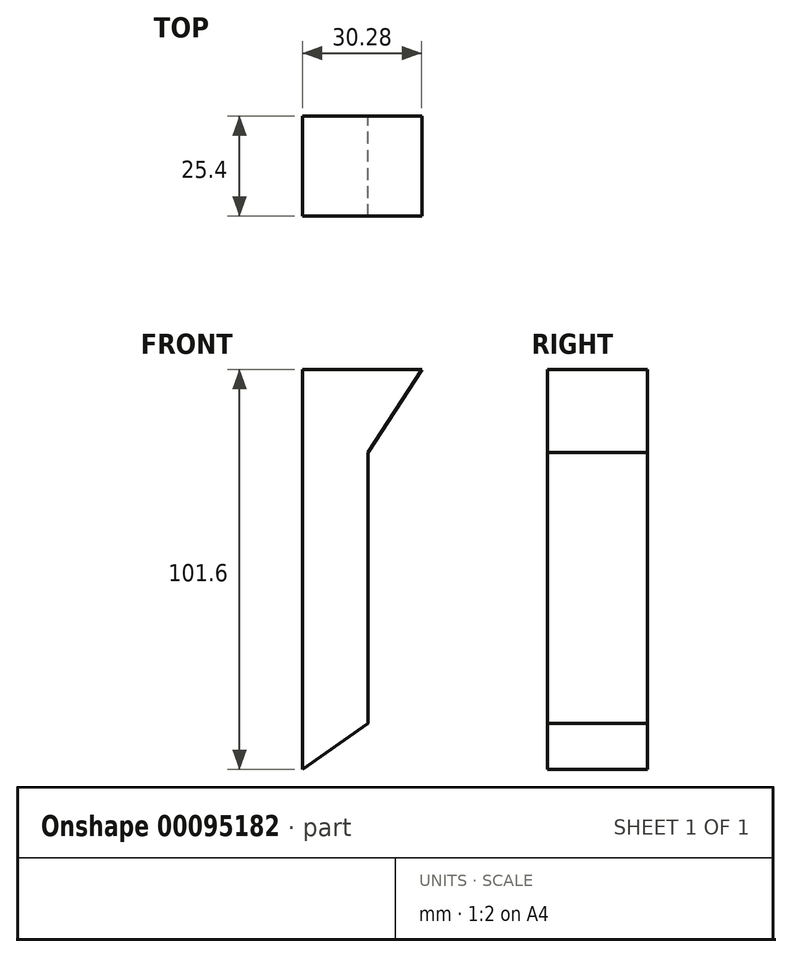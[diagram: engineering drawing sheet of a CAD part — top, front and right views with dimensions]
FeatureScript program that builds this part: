
annotation { "Feature Type Name" : "Feature", "Feature Type Description" : "" }
export const myFeature = defineFeature(function(context is Context, id is Id, definition is map)
    precondition{}
    {
        {
            var Q0;
            Q0=qCreatedBy(makeId("Front.planeOp"),FACE);
            var sketch = newSketch(context, id + "F0", { "sketchPlane" : qUnion([Q0])});
            skLineSegment(sketch, "E0", {"start": v(0, 76.84) * mm, "end": v(0, -24.76) * mm});
            skLineSegment(sketch, "E1", {"start": v(0, -24.76) * mm, "end": v(16.66, -13.1) * mm});
            skLineSegment(sketch, "E2", {"start": v(16.66, -13.1) * mm, "end": v(16.66, 55.8) * mm});
            skLineSegment(sketch, "E3", {"start": v(16.66, 55.8) * mm, "end": v(30.28, 76.84) * mm});
            skLineSegment(sketch, "E4", {"start": v(30.28, 76.84) * mm, "end": v(0, 76.84) * mm});
            skSolve(sketch);
        }
        {
            var Q0;
            Q0 = qSketchRegion(id + "F0", true);
            extrude(context, id + "F1", {"entities" : qUnion([Q0]), "endBound" : BoundingType.SYMMETRIC, "depth" : 25.4 * mm});
        }
    });
